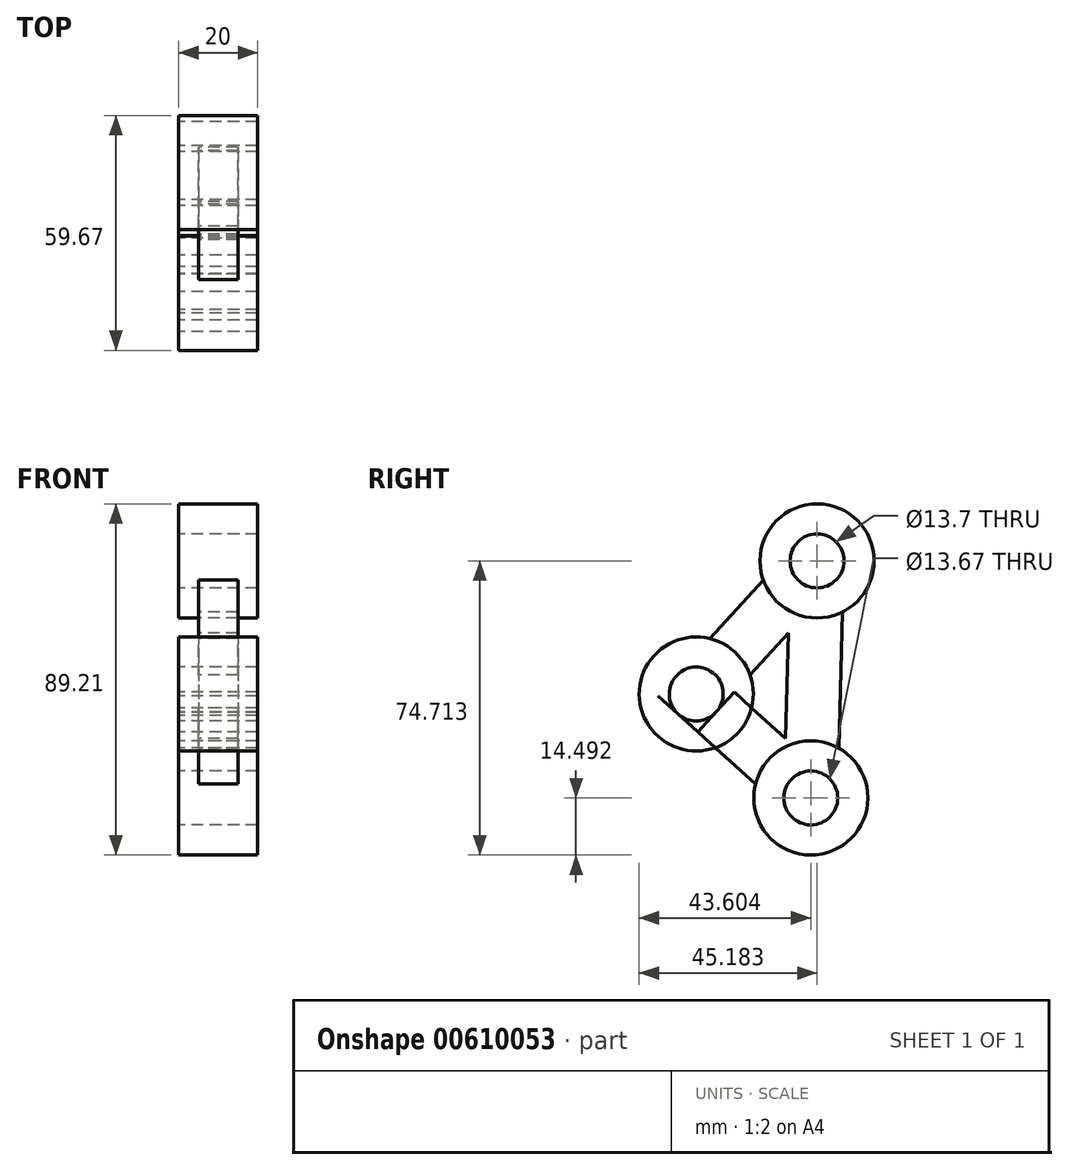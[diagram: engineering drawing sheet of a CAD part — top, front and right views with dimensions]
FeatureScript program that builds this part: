
annotation { "Feature Type Name" : "Feature", "Feature Type Description" : "" }
export const myFeature = defineFeature(function(context is Context, id is Id, definition is map)
    precondition{}
    {
        {
            var Q0;
            Q0=qCreatedBy(makeId("Right.planeOp"),FACE);
            var sketch = newSketch(context, id + "F0", { "sketchPlane" : qUnion([Q0])});
            skCircle(sketch, "E0", {"center": v(0, 0) * mm, "radius": 14.5 * mm});
            skCircle(sketch, "E1", {"center": v(0, 0) * mm, "radius": 6.85 * mm});
            skLineSegment(sketch, "E2", {"start": v(-4.12, -5.47) * mm, "end": v(-14.06, 3.51) * mm});
            skLineSegment(sketch, "E3", {"start": v(-14.06, 3.51) * mm, "end": v(4.85, -13.66) * mm});
            skLineSegment(sketch, "E4", {"start": v(14.06, -3.51) * mm, "end": v(-4.85, 13.66) * mm});
            skLineSegment(sketch, "E5", {"start": v(13.66, 4.85) * mm, "end": v(-3.51, -14.06) * mm});
            skLineSegment(sketch, "E6", {"start": v(-13.66, -4.85) * mm, "end": v(3.51, 14.06) * mm});
            skLineSegment(sketch, "E7", {"start": v(-0.47, 9.68) * mm, "end": v(25.62, 38.42) * mm});
            skLineSegment(sketch, "E8", {"start": v(25.62, 38.42) * mm, "end": v(35.77, 29.2) * mm});
            skLineSegment(sketch, "E9", {"start": v(35.77, 29.2) * mm, "end": v(9.25, 0) * mm});
            skLineSegment(sketch, "E10", {"start": v(-4.12, -5.47) * mm, "end": v(24.52, -31.47) * mm});
            skLineSegment(sketch, "E11", {"start": v(24.52, -31.47) * mm, "end": v(33.7, -21.35) * mm});
            skLineSegment(sketch, "E12", {"start": v(33.7, -21.35) * mm, "end": v(14.06, -3.51) * mm});
            skCircle(sketch, "E13", {"center": v(29.11, -26.4) * mm, "radius": 6.84 * mm});
            skCircle(sketch, "E14", {"center": v(30.7, 33.81) * mm, "radius": 6.85 * mm});
            skLineSegment(sketch, "E15", {"start": v(30.7, 33.81) * mm, "end": v(29.11, -26.4) * mm});
            skLineSegment(sketch, "E16", {"start": v(23.84, 33.81) * mm, "end": v(22.27, -26.4) * mm});
            skLineSegment(sketch, "E17", {"start": v(37.54, 33.81) * mm, "end": v(35.95, -26.4) * mm});
            skLineSegment(sketch, "E18", {"start": v(37.54, 33.81) * mm, "end": v(23.84, 33.81) * mm});
            skCircle(sketch, "E19", {"center": v(30.7, 33.81) * mm, "radius": 14.5 * mm});
            skCircle(sketch, "E20", {"center": v(29.11, -26.4) * mm, "radius": 14.5 * mm});
            skSolve(sketch);
        }
        {
            var Q0;
            {var subQ0=sQuery(id+"F0.wireOp",EDGE,"E4");var subQ1=sQuery(id+"F0.wireOp",EDGE,"E0");var subQ2=makeQuery(id+"F0.imprint","INTERSECT",VERTEX,{"derivedFrom":[subQ1,subQ0]});Q0=makeQuery(id+"F0.imprint","IMPRINT",FACE,{"disambiguationData":[TD([[makeQuery(id+"F0.imprint","IMPRINT",EDGE,{"disambiguationData":[TD([[subQ2,1.0]])],"derivedFrom":subQ1}),1.0]])]});}
            var Q1;
            {var subQ1=sQuery(id+"F0.wireOp",EDGE,"E0");var subQ3=sQuery(id+"F0.wireOp",EDGE,"E6");var subQ4=makeQuery(id+"F0.imprint","INTERSECT",VERTEX,{"derivedFrom":[subQ1,subQ3]});Q1=makeQuery(id+"F0.imprint","IMPRINT",FACE,{"disambiguationData":[TD([[makeQuery(id+"F0.imprint","IMPRINT",EDGE,{"disambiguationData":[TD([[subQ4,-1.0]])],"derivedFrom":subQ3}),1.0]])]});}
            var Q2;
            {var subQ0=sQuery(id+"F0.wireOp",EDGE,"E3");var subQ1=sQuery(id+"F0.wireOp",EDGE,"E0");var subQ2=makeQuery(id+"F0.imprint","INTERSECT",VERTEX,{"derivedFrom":[subQ1,subQ0]});Q2=makeQuery(id+"F0.imprint","IMPRINT",FACE,{"disambiguationData":[TD([[makeQuery(id+"F0.imprint","IMPRINT",EDGE,{"disambiguationData":[TD([[subQ2,1.0]])],"derivedFrom":subQ1}),1.0]])]});}
            var Q3;
            {var subQ0=sQuery(id+"F0.wireOp",EDGE,"E3");var subQ1=sQuery(id+"F0.wireOp",EDGE,"E0");var subQ2=makeQuery(id+"F0.imprint","INTERSECT",VERTEX,{"derivedFrom":[subQ1,subQ0]});Q3=makeQuery(id+"F0.imprint","IMPRINT",FACE,{"disambiguationData":[TD([[makeQuery(id+"F0.imprint","IMPRINT",EDGE,{"disambiguationData":[TD([[subQ2,-1.0]])],"derivedFrom":subQ1}),1.0]])]});}
            var Q4;
            {var subQ1=sQuery(id+"F0.wireOp",EDGE,"E2");var subQ3=sQuery(id+"F0.wireOp",EDGE,"E6");var subQ4=makeQuery(id+"F0.imprint","INTERSECT",VERTEX,{"derivedFrom":[subQ1,subQ3]});Q4=makeQuery(id+"F0.imprint","IMPRINT",FACE,{"disambiguationData":[TD([[makeQuery(id+"F0.imprint","IMPRINT",EDGE,{"disambiguationData":[TD([[subQ4,1.0]])],"derivedFrom":subQ3}),1.0]])]});}
            var Q5;
            {var subQ0=sQuery(id+"F0.wireOp",EDGE,"E13");var subQ5=sQuery(id+"F0.wireOp",EDGE,"E17");var subQ7=makeQuery(id+"F0.imprint","INTERSECT",VERTEX,{"derivedFrom":[subQ0,subQ5]});Q5=makeQuery(id+"F0.imprint","IMPRINT",FACE,{"disambiguationData":[TD([[makeQuery(id+"F0.imprint","IMPRINT",EDGE,{"disambiguationData":[TD([[subQ7,1.0]])],"derivedFrom":subQ5}),1.0]])]});}
            var Q6;
            {var subQ3=sQuery(id+"F0.wireOp",EDGE,"E6");var subQ5=makeQuery(id+"F0.imprint","INTERSECT",VERTEX,{"derivedFrom":[sQuery(id+"F0.wireOp",EDGE,"E1"),subQ3]});Q6=makeQuery(id+"F0.imprint","IMPRINT",FACE,{"disambiguationData":[TD([[makeQuery(id+"F0.imprint","IMPRINT",EDGE,{"disambiguationData":[TD([[subQ5,1.0]])],"derivedFrom":subQ3}),1.0]])]});}
            var Q7;
            {var subQ2=sQuery(id+"F0.wireOp",EDGE,"E5");var subQ4=sQuery(id+"F0.wireOp",EDGE,"E0");var subQ5=makeQuery(id+"F0.imprint","INTERSECT",VERTEX,{"derivedFrom":[subQ4,subQ2]});Q7=makeQuery(id+"F0.imprint","IMPRINT",FACE,{"disambiguationData":[TD([[makeQuery(id+"F0.imprint","IMPRINT",EDGE,{"disambiguationData":[TD([[subQ5,1.0]])],"derivedFrom":subQ4}),1.0]])]});}
            var Q8;
            {var subQ0=sQuery(id+"F0.wireOp",EDGE,"E19");var subQ1=sQuery(id+"F0.wireOp",EDGE,"E17");var subQ2=makeQuery(id+"F0.imprint","INTERSECT",VERTEX,{"derivedFrom":[subQ1,subQ0]});Q8=makeQuery(id+"F0.imprint","IMPRINT",FACE,{"disambiguationData":[TD([[makeQuery(id+"F0.imprint","IMPRINT",EDGE,{"disambiguationData":[TD([[subQ2,1.0]])],"derivedFrom":subQ1}),1.0]])]});}
            var Q9;
            {var subQ1=sQuery(id+"F0.wireOp",EDGE,"E7");var subQ3=sQuery(id+"F0.wireOp",EDGE,"E19");var subQ4=makeQuery(id+"F0.imprint","INTERSECT",VERTEX,{"derivedFrom":[subQ1,subQ3]});Q9=makeQuery(id+"F0.imprint","IMPRINT",FACE,{"disambiguationData":[TD([[makeQuery(id+"F0.imprint","IMPRINT",EDGE,{"disambiguationData":[TD([[subQ4,-1.0]])],"derivedFrom":subQ3}),1.0]])]});}
            var Q10;
            {var subQ0=sQuery(id+"F0.wireOp",EDGE,"E13");var subQ5=sQuery(id+"F0.wireOp",EDGE,"E16");var subQ6=makeQuery(id+"F0.imprint","INTERSECT",VERTEX,{"derivedFrom":[subQ0,subQ5]});Q10=makeQuery(id+"F0.imprint","IMPRINT",FACE,{"disambiguationData":[TD([[makeQuery(id+"F0.imprint","IMPRINT",EDGE,{"disambiguationData":[TD([[subQ6,1.0]])],"derivedFrom":subQ5}),-1.0]])]});}
            var Q11;
            {var subQ0=sQuery(id+"F0.wireOp",EDGE,"E7");var subQ3=sQuery(id+"F0.wireOp",EDGE,"E0");var subQ4=makeQuery(id+"F0.imprint","INTERSECT",VERTEX,{"derivedFrom":[subQ3,subQ0]});Q11=makeQuery(id+"F0.imprint","IMPRINT",FACE,{"disambiguationData":[TD([[makeQuery(id+"F0.imprint","IMPRINT",EDGE,{"disambiguationData":[TD([[subQ4,1.0]])],"derivedFrom":subQ3}),1.0]])]});}
            var Q12;
            {var subQ0=sQuery(id+"F0.wireOp",EDGE,"E9");var subQ1=sQuery(id+"F0.wireOp",EDGE,"E5");var subQ2=makeQuery(id+"F0.imprint","INTERSECT",VERTEX,{"derivedFrom":[subQ1,subQ0]});Q12=makeQuery(id+"F0.imprint","IMPRINT",FACE,{"disambiguationData":[TD([[makeQuery(id+"F0.imprint","IMPRINT",EDGE,{"disambiguationData":[TD([[subQ2,-1.0]])],"derivedFrom":subQ1}),1.0]])]});}
            var Q13;
            {var subQ0=sQuery(id+"F0.wireOp",EDGE,"E15");var subQ1=sQuery(id+"F0.wireOp",EDGE,"E12");var subQ2=makeQuery(id+"F0.imprint","INTERSECT",VERTEX,{"derivedFrom":[subQ1,subQ0]});Q13=makeQuery(id+"F0.imprint","IMPRINT",FACE,{"disambiguationData":[TD([[makeQuery(id+"F0.imprint","IMPRINT",EDGE,{"disambiguationData":[TD([[subQ2,1.0]])],"derivedFrom":subQ0}),1.0]])]});}
            var Q14;
            {var subQ0=sQuery(id+"F0.wireOp",EDGE,"E15");var subQ1=sQuery(id+"F0.wireOp",EDGE,"E12");var subQ2=makeQuery(id+"F0.imprint","INTERSECT",VERTEX,{"derivedFrom":[subQ1,subQ0]});Q14=makeQuery(id+"F0.imprint","IMPRINT",FACE,{"disambiguationData":[TD([[makeQuery(id+"F0.imprint","IMPRINT",EDGE,{"disambiguationData":[TD([[subQ2,-1.0]])],"derivedFrom":subQ1}),1.0]])]});}
            var Q15;
            {var subQ0=sQuery(id+"F0.wireOp",EDGE,"E15");var subQ1=sQuery(id+"F0.wireOp",EDGE,"E12");var subQ2=makeQuery(id+"F0.imprint","INTERSECT",VERTEX,{"derivedFrom":[subQ1,subQ0]});Q15=makeQuery(id+"F0.imprint","IMPRINT",FACE,{"disambiguationData":[TD([[makeQuery(id+"F0.imprint","IMPRINT",EDGE,{"disambiguationData":[TD([[subQ2,-1.0]])],"derivedFrom":subQ1}),-1.0]])]});}
            var Q16;
            {var subQ1=sQuery(id+"F0.wireOp",EDGE,"E12");var subQ3=sQuery(id+"F0.wireOp",EDGE,"E15");var subQ4=makeQuery(id+"F0.imprint","INTERSECT",VERTEX,{"derivedFrom":[subQ1,subQ3]});Q16=makeQuery(id+"F0.imprint","IMPRINT",FACE,{"disambiguationData":[TD([[makeQuery(id+"F0.imprint","IMPRINT",EDGE,{"disambiguationData":[TD([[subQ4,-1.0]])],"derivedFrom":subQ3}),1.0]])]});}
            var Q17;
            {var subQ0=sQuery(id+"F0.wireOp",EDGE,"E4");var subQ1=sQuery(id+"F0.wireOp",EDGE,"E1");var subQ2=makeQuery(id+"F0.imprint","INTERSECT",VERTEX,{"derivedFrom":[subQ1,subQ0]});Q17=makeQuery(id+"F0.imprint","IMPRINT",FACE,{"disambiguationData":[TD([[makeQuery(id+"F0.imprint","IMPRINT",EDGE,{"disambiguationData":[TD([[subQ2,1.0]])],"derivedFrom":subQ1}),-1.0]])]});}
            var Q18;
            {var subQ5=sQuery(id+"F0.wireOp",EDGE,"E15");var subQ7=sQuery(id+"F0.wireOp",EDGE,"E9");var subQ8=makeQuery(id+"F0.imprint","INTERSECT",VERTEX,{"derivedFrom":[subQ7,subQ5]});Q18=makeQuery(id+"F0.imprint","IMPRINT",FACE,{"disambiguationData":[TD([[makeQuery(id+"F0.imprint","IMPRINT",EDGE,{"disambiguationData":[TD([[subQ8,-1.0]])],"derivedFrom":subQ7}),-1.0]])]});}
            var Q19;
            {var subQ0=sQuery(id+"F0.wireOp",EDGE,"E15");var subQ1=sQuery(id+"F0.wireOp",EDGE,"E9");var subQ2=makeQuery(id+"F0.imprint","INTERSECT",VERTEX,{"derivedFrom":[subQ1,subQ0]});Q19=makeQuery(id+"F0.imprint","IMPRINT",FACE,{"disambiguationData":[TD([[makeQuery(id+"F0.imprint","IMPRINT",EDGE,{"disambiguationData":[TD([[subQ2,-1.0]])],"derivedFrom":subQ0}),1.0]])]});}
            var Q20;
            {var subQ0=sQuery(id+"F0.wireOp",EDGE,"E15");var subQ1=sQuery(id+"F0.wireOp",EDGE,"E9");var subQ2=makeQuery(id+"F0.imprint","INTERSECT",VERTEX,{"derivedFrom":[subQ1,subQ0]});Q20=makeQuery(id+"F0.imprint","IMPRINT",FACE,{"disambiguationData":[TD([[makeQuery(id+"F0.imprint","IMPRINT",EDGE,{"disambiguationData":[TD([[subQ2,-1.0]])],"derivedFrom":subQ1}),1.0]])]});}
            var Q21;
            {var subQ0=sQuery(id+"F0.wireOp",EDGE,"E6");var subQ1=sQuery(id+"F0.wireOp",EDGE,"E1");var subQ2=makeQuery(id+"F0.imprint","INTERSECT",VERTEX,{"derivedFrom":[subQ1,subQ0]});Q21=makeQuery(id+"F0.imprint","IMPRINT",FACE,{"disambiguationData":[TD([[makeQuery(id+"F0.imprint","IMPRINT",EDGE,{"disambiguationData":[TD([[subQ2,1.0]])],"derivedFrom":subQ1}),-1.0]])]});}
            var Q22;
            {var subQ1=sQuery(id+"F0.wireOp",EDGE,"E1");var subQ3=sQuery(id+"F0.wireOp",EDGE,"E5");var subQ4=makeQuery(id+"F0.imprint","INTERSECT",VERTEX,{"derivedFrom":[subQ1,subQ3]});Q22=makeQuery(id+"F0.imprint","IMPRINT",FACE,{"disambiguationData":[TD([[makeQuery(id+"F0.imprint","IMPRINT",EDGE,{"disambiguationData":[TD([[subQ4,-1.0]])],"derivedFrom":subQ3}),-1.0]])]});}
            var Q23;
            {var subQ0=sQuery(id+"F0.wireOp",EDGE,"E6");var subQ1=sQuery(id+"F0.wireOp",EDGE,"E1");var subQ2=makeQuery(id+"F0.imprint","INTERSECT",VERTEX,{"derivedFrom":[subQ1,subQ0]});Q23=makeQuery(id+"F0.imprint","IMPRINT",FACE,{"disambiguationData":[TD([[makeQuery(id+"F0.imprint","IMPRINT",EDGE,{"disambiguationData":[TD([[subQ2,-1.0]])],"derivedFrom":subQ1}),-1.0]])]});}
            var Q24;
            {var subQ1=sQuery(id+"F0.wireOp",EDGE,"E0");var subQ3=sQuery(id+"F0.wireOp",EDGE,"E9");var subQ4=makeQuery(id+"F0.imprint","INTERSECT",VERTEX,{"derivedFrom":[subQ1,subQ3]});Q24=makeQuery(id+"F0.imprint","IMPRINT",FACE,{"disambiguationData":[TD([[makeQuery(id+"F0.imprint","IMPRINT",EDGE,{"disambiguationData":[TD([[subQ4,-1.0]])],"derivedFrom":subQ3}),1.0]])]});}
            var Q25;
            {var subQ1=sQuery(id+"F0.wireOp",EDGE,"E9");var subQ3=sQuery(id+"F0.wireOp",EDGE,"E15");var subQ4=makeQuery(id+"F0.imprint","INTERSECT",VERTEX,{"derivedFrom":[subQ1,subQ3]});Q25=makeQuery(id+"F0.imprint","IMPRINT",FACE,{"disambiguationData":[TD([[makeQuery(id+"F0.imprint","IMPRINT",EDGE,{"disambiguationData":[TD([[subQ4,1.0]])],"derivedFrom":subQ3}),1.0]])]});}
            extrude(context, id + "F1", {"entities" : qUnion([Q0, Q1, Q2, Q3, Q4, Q5, Q6, Q7, Q8, Q9, Q10, Q11, Q12, Q13, Q14, Q15, Q16, Q17, Q18, Q19, Q20, Q21, Q22, Q23, Q24, Q25]), "endBound" : BoundingType.SYMMETRIC, "depth" : 20 * mm, "offsetDistance" : 25.4 * mm});
        }
        {
            var Q0;
            {var subQ0=sQuery(id+"F0.wireOp",EDGE,"E19");var subQ1=sQuery(id+"F0.wireOp",EDGE,"E15");var subQ2=makeQuery(id+"F0.imprint","INTERSECT",VERTEX,{"derivedFrom":[subQ1,subQ0]});Q0=makeQuery(id+"F0.imprint","IMPRINT",FACE,{"disambiguationData":[TD([[makeQuery(id+"F0.imprint","IMPRINT",EDGE,{"disambiguationData":[TD([[subQ2,-1.0]])],"derivedFrom":subQ1}),1.0]])]});}
            var Q1;
            {var subQ1=sQuery(id+"F0.wireOp",EDGE,"E9");var subQ7=sQuery(id+"F0.wireOp",EDGE,"E19");var subQ8=makeQuery(id+"F0.imprint","INTERSECT",VERTEX,{"derivedFrom":[subQ1,subQ7]});Q1=makeQuery(id+"F0.imprint","IMPRINT",FACE,{"disambiguationData":[TD([[makeQuery(id+"F0.imprint","IMPRINT",EDGE,{"disambiguationData":[TD([[subQ8,-1.0]])],"derivedFrom":subQ1}),1.0]])]});}
            var Q2;
            {var subQ5=sQuery(id+"F0.wireOp",EDGE,"E0");var subQ7=sQuery(id+"F0.wireOp",EDGE,"E10");var subQ8=makeQuery(id+"F0.imprint","INTERSECT",VERTEX,{"derivedFrom":[subQ5,subQ7]});Q2=makeQuery(id+"F0.imprint","IMPRINT",FACE,{"disambiguationData":[TD([[makeQuery(id+"F0.imprint","IMPRINT",EDGE,{"disambiguationData":[TD([[subQ8,-1.0]])],"derivedFrom":subQ7}),1.0]])]});}
            var Q3;
            {var subQ5=sQuery(id+"F0.wireOp",EDGE,"E0");var subQ7=sQuery(id+"F0.wireOp",EDGE,"E7");var subQ8=makeQuery(id+"F0.imprint","INTERSECT",VERTEX,{"derivedFrom":[subQ5,subQ7]});Q3=makeQuery(id+"F0.imprint","IMPRINT",FACE,{"disambiguationData":[TD([[makeQuery(id+"F0.imprint","IMPRINT",EDGE,{"disambiguationData":[TD([[subQ8,1.0]])],"derivedFrom":subQ5}),-1.0]])]});}
            var Q4;
            {var subQ0=sQuery(id+"F0.wireOp",EDGE,"E19");var subQ1=sQuery(id+"F0.wireOp",EDGE,"E9");var subQ2=makeQuery(id+"F0.imprint","INTERSECT",VERTEX,{"derivedFrom":[subQ1,subQ0]});Q4=makeQuery(id+"F0.imprint","IMPRINT",FACE,{"disambiguationData":[TD([[makeQuery(id+"F0.imprint","IMPRINT",EDGE,{"disambiguationData":[TD([[subQ2,-1.0]])],"derivedFrom":subQ1}),-1.0]])]});}
            var Q5;
            {var subQ0=sQuery(id+"F0.wireOp",EDGE,"E20");var subQ1=sQuery(id+"F0.wireOp",EDGE,"E12");var subQ2=makeQuery(id+"F0.imprint","INTERSECT",VERTEX,{"derivedFrom":[subQ1,subQ0]});Q5=makeQuery(id+"F0.imprint","IMPRINT",FACE,{"disambiguationData":[TD([[makeQuery(id+"F0.imprint","IMPRINT",EDGE,{"disambiguationData":[TD([[subQ2,-1.0]])],"derivedFrom":subQ1}),1.0]])]});}
            extrude(context, id + "F2", {"entities" : qUnion([Q0, Q1, Q2, Q3, Q4, Q5]), "endBound" : BoundingType.SYMMETRIC, "depth" : 10 * mm, "offsetDistance" : 25 * mm});
        }
    });
